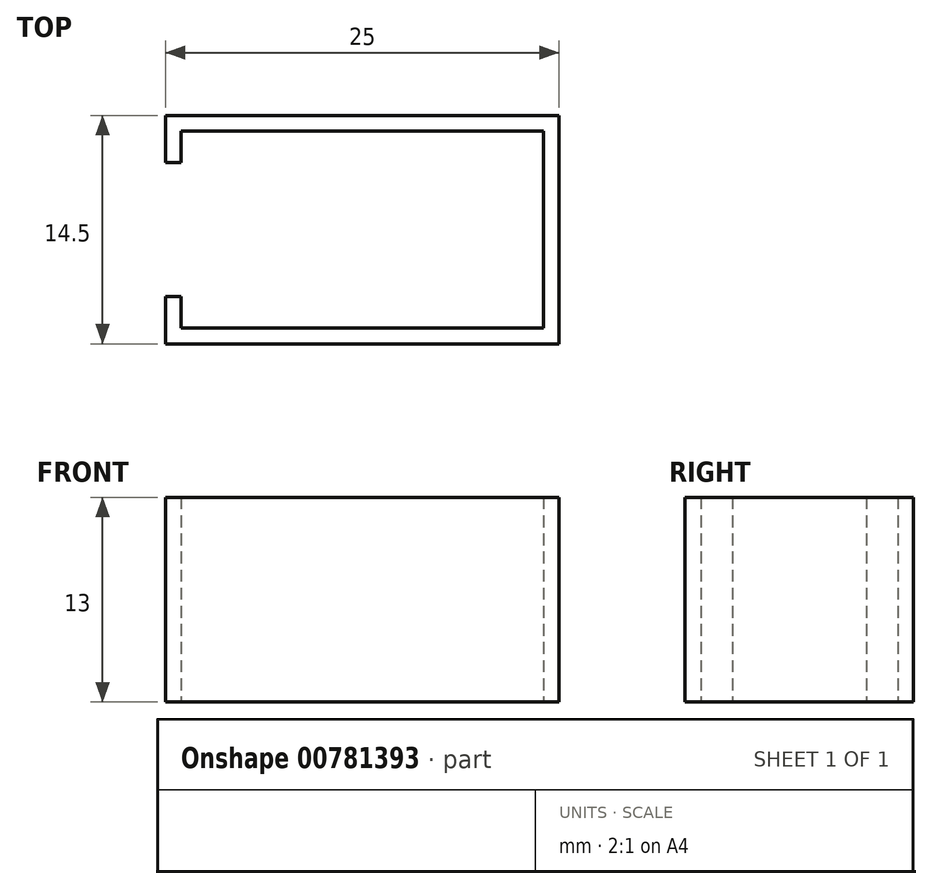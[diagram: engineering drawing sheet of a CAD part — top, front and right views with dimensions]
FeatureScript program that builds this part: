
annotation { "Feature Type Name" : "Feature", "Feature Type Description" : "" }
export const myFeature = defineFeature(function(context is Context, id is Id, definition is map)
    precondition{}
    {
        {
            var Q0;
            Q0=qCreatedBy(makeId("Top.planeOp"),FACE);
            var sketch = newSketch(context, id + "F0", { "sketchPlane" : qUnion([Q0])});
            skLineSegment(sketch, "E0.bottom", {"start": v(-11.5, -6.25) * mm, "end": v(11.5, -6.25) * mm});
            skLineSegment(sketch, "E0.top", {"start": v(-11.5, 6.25) * mm, "end": v(11.5, 6.25) * mm});
            skLineSegment(sketch, "E0.left", {"start": v(-11.5, -6.25) * mm, "end": v(-11.5, 6.25) * mm});
            skLineSegment(sketch, "E0.right", {"start": v(11.5, -6.25) * mm, "end": v(11.5, 6.25) * mm});
            skLineSegment(sketch, "E1.bottom", {"start": v(-12.5, -7.25) * mm, "end": v(12.5, -7.25) * mm});
            skLineSegment(sketch, "E1.top", {"start": v(-12.5, 7.25) * mm, "end": v(12.5, 7.25) * mm});
            skLineSegment(sketch, "E1.left", {"start": v(-12.5, -7.25) * mm, "end": v(-12.5, 7.25) * mm});
            skLineSegment(sketch, "E1.right", {"start": v(12.5, -7.25) * mm, "end": v(12.5, 7.25) * mm});
            skSolve(sketch);
        }
        {
            var Q0;
            Q0=makeQuery(id+"F0.imprint","IMPRINT",FACE,{"disambiguationData":[TD([[makeQuery(id+"F0.imprint","IMPRINT",EDGE,{"derivedFrom":sQuery(id+"F0.wireOp",EDGE,"E0.bottom")}),-1.0]])]});
            extrude(context, id + "F1", {"entities" : qUnion([Q0]), "depth" : 13 * mm, "offsetDistance" : 25 * mm});
        }
        {
            var Q0;
            Q0=makeQuery(id+"F1.opExtrude","SWEPT_FACE",FACE,{"disambiguationData":[OSD([sQuery(id+"F0.wireOp",EDGE,"E1.left")])]});
            var sketch = newSketch(context, id + "F2", { "sketchPlane" : qUnion([Q0])});
            skLineSegment(sketch, "E2.bottom", {"start": v(-4.25, 13) * mm, "end": v(4.25, 13) * mm});
            skLineSegment(sketch, "E2.top", {"start": v(-4.25, 0) * mm, "end": v(4.25, 0) * mm});
            skLineSegment(sketch, "E2.left", {"start": v(-4.25, 13) * mm, "end": v(-4.25, 0) * mm});
            skLineSegment(sketch, "E2.right", {"start": v(4.25, 13) * mm, "end": v(4.25, 0) * mm});
            skSolve(sketch);
        }
        {
            var Q0;
            Q0=makeQuery(id+"F2.imprint","IMPRINT",FACE,{"disambiguationData":[TD([[makeQuery(id+"F2.imprint","IMPRINT",EDGE,{"derivedFrom":sQuery(id+"F2.wireOp",EDGE,"E2.bottom")}),1.0]])]});
            extrude(context, id + "F3", {"entities" : qUnion([Q0]), "operationType" : NewBodyOperationType.REMOVE, "oppositeDirection" : true, "depth" : 1 * mm, "offsetDistance" : 25 * mm});
        }
    });
